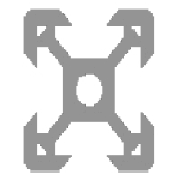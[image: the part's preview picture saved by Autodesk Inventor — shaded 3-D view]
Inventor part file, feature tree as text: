
AUTODESK INVENTOR PART (.ipt)
format: ipt  version: 2013 (Build 170138000, 138)  size: 187,392 bytes
history: native  units: mm
features: other x4, sketch x2, plane x1
ambient origin geometry x8: Origin, YZ Plane, XZ Plane, XY Plane, X Axis, Y Axis, Z Axis, Center Point
bodies: Solid1 (feature_tree), Body (feature_tree)
feature tree (7):
  other  "Driven Length"
  other  "Frame Generator"
  other  "Start Plane"
  other  "End Plane"
  sketch  "Sketch4"  dims[d2=4.2mm]
  plane  "Work Plane4"
  sketch  "Sketch5"  dims[d3=1.5mm d4=1.64mm d5=1.8mm d6=5.68mm d7=1.8mm d9=1.5mm d12=-0.0mm d13=275.0mm d14=0.13mm d15=0.0mm d18=90.0deg d17=275.0mm]
